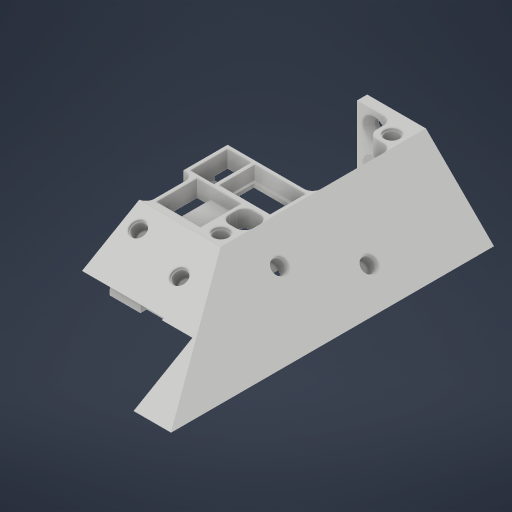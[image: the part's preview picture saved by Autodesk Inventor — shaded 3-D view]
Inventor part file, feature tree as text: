
AUTODESK INVENTOR PART (.ipt)
format: ipt  version: 2023 (Build 270158000, 158)  size: 527,872 bytes
history: native  units: mm
features: sketch x24, extrude x19, hole x6, other x1, fillet x1
ambient origin geometry x8: Origin, YZ Plane, XZ Plane, XY Plane, X Axis, Y Axis, Z Axis, Center Point
bodies: Body1 (feature_tree), Body2 (feature_tree)
feature tree (51):
  other  "Bryła1"
  extrude  "Wyciągnięcie proste1"  Depth=95.0mm
  extrude  "Wyciągnięcie proste2"  Depth=20.0mm
  extrude  "Wyciągnięcie proste3"  Depth=20.0mm TaperAngle=0.0deg
  extrude  "Wyciągnięcie proste4"  TaperAngle=45.0deg  [1 undecoded]
  extrude  "Wyciągnięcie proste5"  Depth=20.0mm TaperAngle=0.0deg
  extrude  "Wyciągnięcie proste6"  TaperAngle=30.0deg  [1 undecoded]
  extrude  "Wyciągnięcie proste7"  Depth=20.0mm TaperAngle=0.0deg
  hole  "Otwór1"  [1 undecoded]
  extrude  "Wyciągnięcie proste8"  Depth=9.0mm
  extrude  "Wyciągnięcie proste9"  Depth=24.0mm TaperAngle=0.0deg
  extrude  "Wyciągnięcie proste10"  Depth=9.0mm
  hole  "Otwór2"  [1 undecoded]
  hole  "Otwór3"  [1 undecoded]
  extrude  "Wyciągnięcie proste13"  Depth=1.5mm TaperAngle=0.0deg
  hole  "Otwór4"  [1 undecoded]
  hole  "Otwór5"  [1 undecoded]
  extrude  "Wyciągnięcie proste14"  Depth=15.358897mm
  extrude  "Wyciągnięcie proste15"  Depth=20.0mm TaperAngle=0.0deg
  extrude  "Wyciągnięcie proste16"  Depth=65.0mm
  extrude  "Wyciągnięcie proste17"  Depth=9.26mm
  extrude  "Wyciągnięcie proste18"  Depth=5.0mm
  extrude  "Wyciągnięcie proste19"  Depth=9.26mm
  sketch  "Szkic27"
  extrude  "Wyciągnięcie proste21"  Depth=20.0mm TaperAngle=0.0deg
  extrude  "Wyciągnięcie proste22"  TaperAngle=90.0deg  [1 undecoded]
  hole  "Otwór6"  [1 undecoded]
  fillet  "Fillet1"  Radius=5.0mm
  sketch  "Szkic1"
  sketch  "Szkic2"
  sketch  "Szkic3"
  sketch  "Szkic4"
  sketch  "Szkic5"
  sketch  "Szkic6"
  sketch  "Szkic7"
  sketch  "Szkic8"
  sketch  "Szkic9"
  sketch  "Szkic11"
  sketch  "Szkic12"
  sketch  "Szkic13"
  sketch  "Szkic14"
  sketch  "Szkic17"
  sketch  "Szkic18"
  sketch  "Szkic19"
  sketch  "Szkic21"
  sketch  "Szkic22"
  sketch  "Szkic23"
  sketch  "Szkic24"
  sketch  "Szkic25"
  sketch  "Szkic26"
  sketch  "Szkic29"
note: 9 required parameter values undecoded (feature->parameter linkage not recoverable at this tier; creation-order binding heuristic only, values carry confidence <= 0.55)
